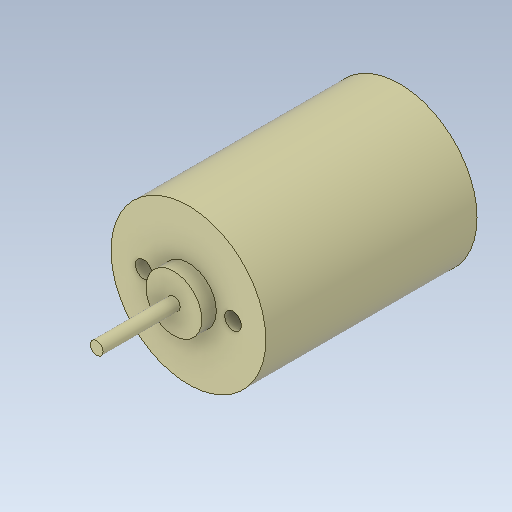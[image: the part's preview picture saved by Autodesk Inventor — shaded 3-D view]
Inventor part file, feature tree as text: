
AUTODESK INVENTOR PART (.ipt)
format: ipt  version: 2020.2 (Build 242310000, 310)  size: 153,600 bytes
history: native  units: mm
features: extrude x5, sketch x5, other x1, hole x1
ambient origin geometry x8: Origin, YZ Plane, XZ Plane, XY Plane, X Axis, Y Axis, Z Axis, Center Point
bodies: Body1 (feature_tree)
feature tree (12):
  other  "ソリッド1"
  extrude  "押し出し1"  Depth=27.7mm
  extrude  "押し出し2"  Depth=37.8mm TaperAngle=0.0deg
  extrude  "押し出し3"  Depth=10.0mm
  sketch  "スケッチ4"
  extrude  "押し出し4"  Depth=2.6mm TaperAngle=0.0deg
  extrude  "押し出し5"  Depth=2.3mm
  hole  "穴1"  [1 undecoded]
  sketch  "スケッチ1"
  sketch  "スケッチ2"
  sketch  "スケッチ3"
  sketch  "スケッチ5"
note: 1 required parameter value undecoded (feature->parameter linkage not recoverable at this tier; creation-order binding heuristic only, values carry confidence <= 0.55)
